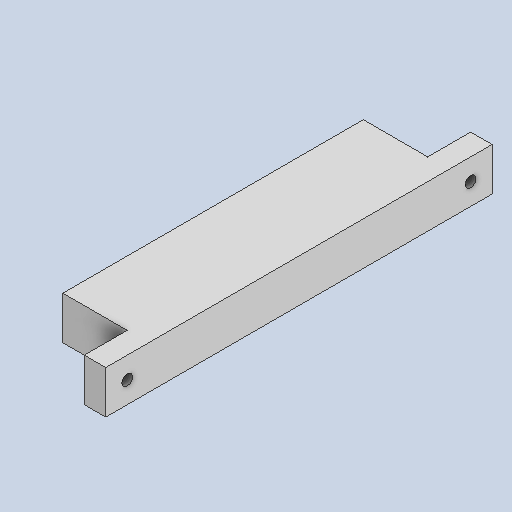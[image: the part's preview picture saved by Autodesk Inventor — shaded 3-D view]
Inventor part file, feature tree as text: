
AUTODESK INVENTOR PART (.ipt)
format: ipt  version: 2023 (Build 270158000, 158)  size: 276,992 bytes
history: native  units: mm
features: thread x4, extrude x3, other x1, sketch x1
ambient origin geometry x8: Origin, YZ Plane, XZ Plane, XY Plane, X Axis, Y Axis, Z Axis, Center Point
bodies: Body1 (feature_tree)
feature tree (9):
  other  "Твердое тело1"
  extrude  "Выдавливание1"  Depth=10.0mm
  extrude  "Выдавливание2"  Depth=20.0mm
  thread  "Резьба4"
  extrude  "Выдавливание3"  Depth=30.0mm
  thread  "Резьба7"
  thread  "Резьба8"
  thread  "Резьба9"
  sketch  "Эскиз3"
